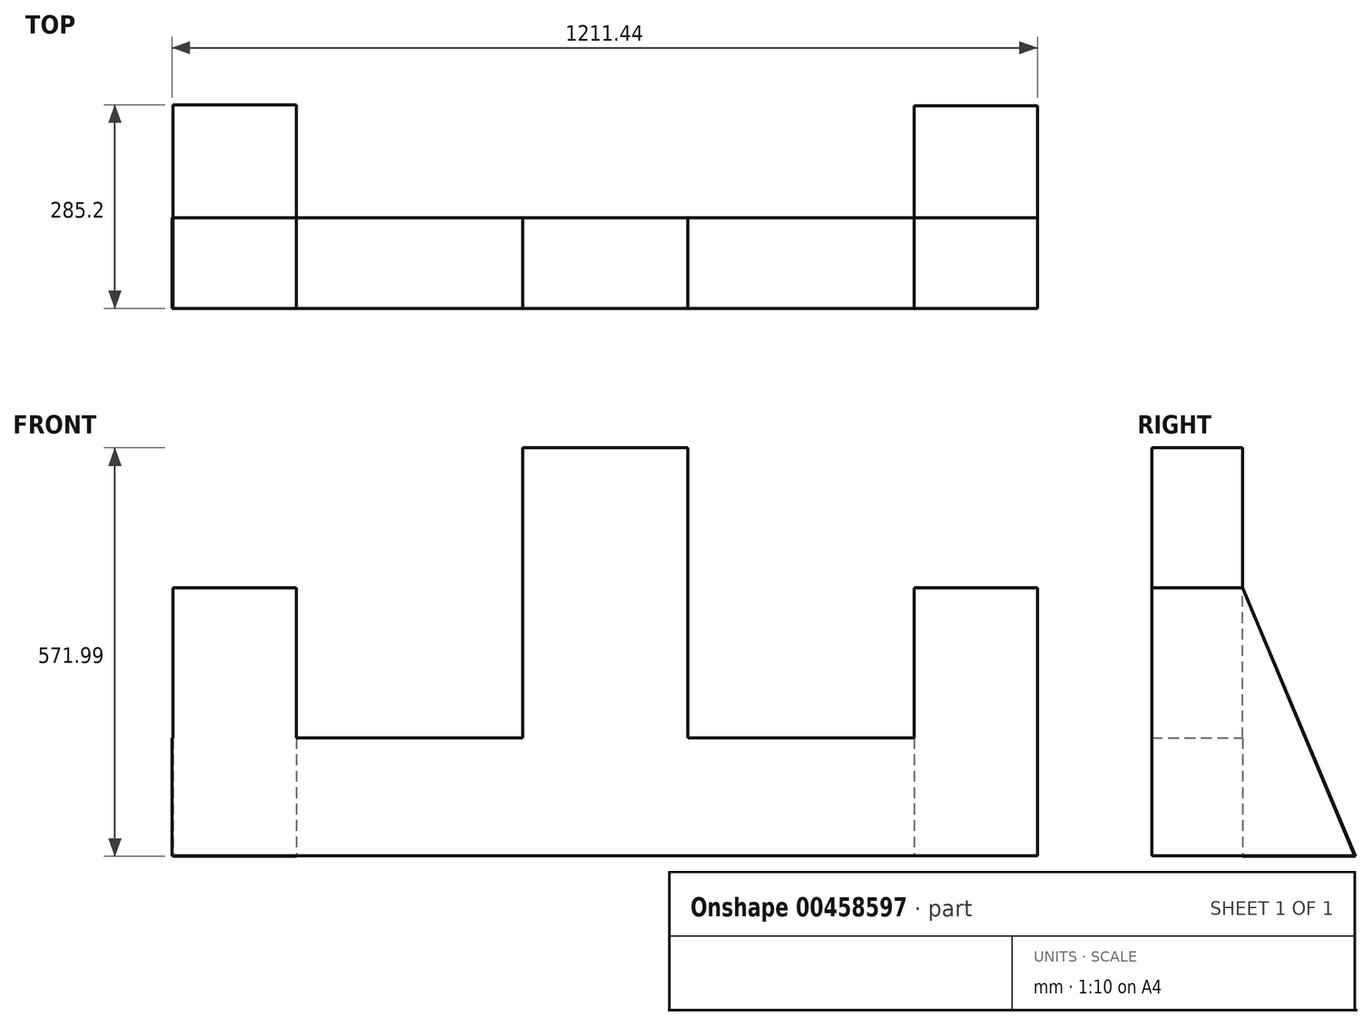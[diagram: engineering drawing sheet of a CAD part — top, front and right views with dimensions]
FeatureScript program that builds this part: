
annotation { "Feature Type Name" : "Feature", "Feature Type Description" : "" }
export const myFeature = defineFeature(function(context is Context, id is Id, definition is map)
    precondition{}
    {
        {
            var Q0;
            Q0=qCreatedBy(makeId("Front.planeOp"),FACE);
            var sketch = newSketch(context, id + "F0", { "sketchPlane" : qUnion([Q0])});
            skLineSegment(sketch, "E0", {"start": v(0, 0) * mm, "end": v(0, -461.78) * mm});
            skLineSegment(sketch, "E1", {"start": v(0, -461.78) * mm, "end": v(605, -461.78) * mm});
            skLineSegment(sketch, "E2", {"start": v(0, -461.78) * mm, "end": v(-606.45, -461.78) * mm});
            skLineSegment(sketch, "E3", {"start": v(-606.45, -461.78) * mm, "end": v(-606.45, -296.65) * mm});
            skLineSegment(sketch, "E4", {"start": v(-606.45, -296.65) * mm, "end": v(0, -296.65) * mm});
            skLineSegment(sketch, "E5", {"start": v(0, -296.65) * mm, "end": v(605, -296.65) * mm});
            skLineSegment(sketch, "E6", {"start": v(605, -296.65) * mm, "end": v(605, -461.78) * mm});
            skLineSegment(sketch, "E7", {"start": v(432.65, -296.65) * mm, "end": v(432.65, -86.2) * mm});
            skLineSegment(sketch, "E8", {"start": v(432.65, -86.2) * mm, "end": v(605, -86.2) * mm});
            skLineSegment(sketch, "E9", {"start": v(605, -86.2) * mm, "end": v(605, -296.65) * mm});
            skLineSegment(sketch, "E10", {"start": v(0, -296.65) * mm, "end": v(-115.4, -296.65) * mm});
            skLineSegment(sketch, "E11", {"start": v(-115.4, -296.65) * mm, "end": v(-115.4, 109.75) * mm});
            skLineSegment(sketch, "E12", {"start": v(-115.4, 109.75) * mm, "end": v(0, 109.75) * mm});
            skLineSegment(sketch, "E13", {"start": v(0, 109.75) * mm, "end": v(0, 0) * mm});
            skLineSegment(sketch, "E14.MirrorCS", {"start": v(115.4, -296.65) * mm, "end": v(115.4, 109.75) * mm});
            skLineSegment(sketch, "E15", {"start": v(115.4, 109.75) * mm, "end": v(0, 109.75) * mm});
            skPoint(sketch, "E16.end.orphan", {"position": v(-463.1, -296.65) * mm});
            skLineSegment(sketch, "E17.MirrorCS", {"start": v(-432.65, -296.65) * mm, "end": v(-432.65, -86.2) * mm});
            skLineSegment(sketch, "E18.MirrorCS", {"start": v(-432.65, -86.2) * mm, "end": v(-605, -86.2) * mm});
            skLineSegment(sketch, "E19.MirrorCS", {"start": v(-605, -86.2) * mm, "end": v(-605, -296.65) * mm});
            skSolve(sketch);
        }
        {
            var Q0;
            Q0 = qSketchRegion(id + "F0", true);
            extrude(context, id + "F1", {"entities" : qUnion([Q0]), "depth" : 127 * mm});
        }
        {
            var Q0;
            Q0=makeQuery(id+"F1.opExtrude","SWEPT_FACE",FACE,{"disambiguationData":[OSD([sQuery(id+"F0.wireOp",EDGE,"E6"),sQuery(id+"F0.wireOp",EDGE,"E9")])]});
            var sketch = newSketch(context, id + "F2", { "sketchPlane" : qUnion([Q0])});
            skLineSegment(sketch, "E20", {"start": v(0, -86.2) * mm, "end": v(157.18, -461.78) * mm});
            skLineSegment(sketch, "E21", {"start": v(157.18, -461.78) * mm, "end": v(0, -461.78) * mm});
            skLineSegment(sketch, "E22", {"start": v(0, -86.2) * mm, "end": v(0, -461.78) * mm});
            skSolve(sketch);
        }
        {
            var Q0;
            Q0=makeQuery(id+"F1.opExtrude","SWEPT_FACE",FACE,{"disambiguationData":[OSD([sQuery(id+"F0.wireOp",EDGE,"E19.MirrorCS")])]});
            var sketch = newSketch(context, id + "F3", { "sketchPlane" : qUnion([Q0])});
            skLineSegment(sketch, "E23", {"start": v(0, -86.2) * mm, "end": v(-158.2, -462.24) * mm});
            skLineSegment(sketch, "E24", {"start": v(-158.2, -462.24) * mm, "end": v(0, -462.24) * mm});
            skLineSegment(sketch, "E25", {"start": v(0, -462.24) * mm, "end": v(0, -86.2) * mm});
            skSolve(sketch);
        }
        {
            var Q0;
            Q0 = qSketchRegion(id + "F3", true);
            extrude(context, id + "F4", {"entities" : qUnion([Q0]), "operationType" : NewBodyOperationType.ADD, "oppositeDirection" : true, "depth" : 172.72 * mm});
        }
        {
            var Q0;
            Q0 = qSketchRegion(id + "F2", true);
            extrude(context, id + "F5", {"entities" : qUnion([Q0]), "operationType" : NewBodyOperationType.ADD, "oppositeDirection" : true, "depth" : 172.72 * mm});
        }
    });
